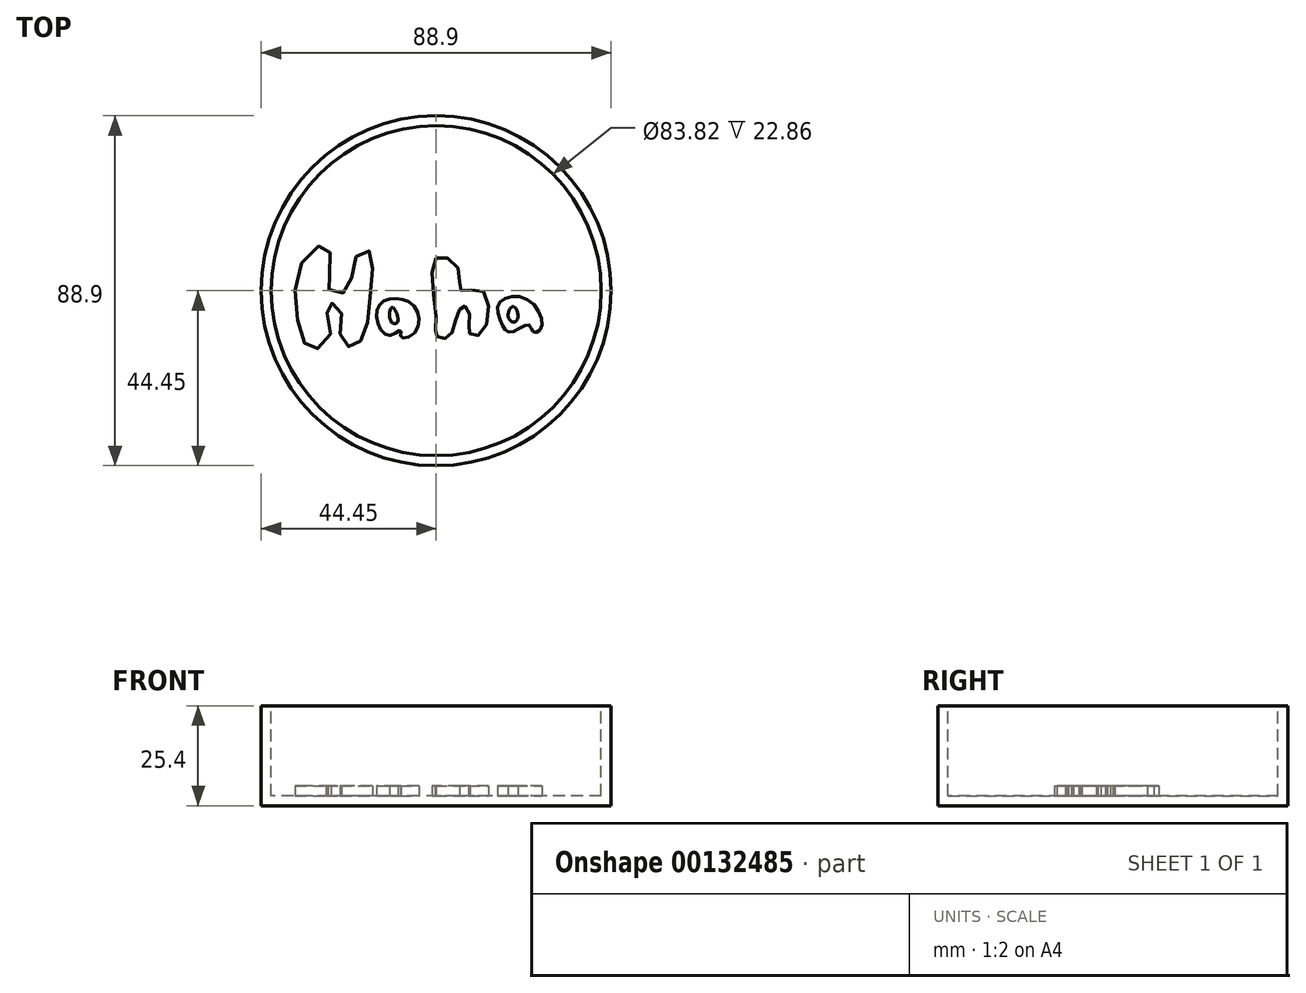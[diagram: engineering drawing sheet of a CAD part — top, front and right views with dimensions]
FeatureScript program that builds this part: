
annotation { "Feature Type Name" : "Feature", "Feature Type Description" : "" }
export const myFeature = defineFeature(function(context is Context, id is Id, definition is map)
    precondition{}
    {
        {
            var Q0;
            Q0=qCreatedBy(makeId("Top.planeOp"),FACE);
            var sketch = newSketch(context, id + "F0", { "sketchPlane" : qUnion([Q0])});
            skCircle(sketch, "E0", {"center": v(0, 0) * mm, "radius": 44.45 * mm});
            skSolve(sketch);
        }
        {
            var Q0;
            Q0=makeQuery(id+"F0.imprint","IMPRINT",FACE,{"disambiguationData":[TD([[makeQuery(id+"F0.imprint","IMPRINT",EDGE,{"derivedFrom":sQuery(id+"F0.wireOp",EDGE,"E0")}),1.0]])]});
            extrude(context, id + "F1", {"entities" : qUnion([Q0]), "oppositeDirection" : true, "depth" : 25.4 * mm});
        }
        {
            var Q0;
            Q0=makeQuery(id+"F1.opExtrude","CAP_FACE",FACE,{"disambiguationData":[OSD([sQuery(id+"F0.wireOp",EDGE,"E0")])],"isStart":true});
            shell(context, id + "F2", {"entities" : qUnion([Q0]), "thickness" : 2.54 * mm});
        }
        {
            var Q0;
            {var subQ0=sQuery(id+"F0.wireOp",EDGE,"E0");Q0=makeQuery(id+"F2.opShell","OFFSET_FACE",FACE,{"disambiguationData":[OSD([subQ0]),TDD([makeQuery(id+"F1.opExtrude","CAP_FACE",FACE,{"disambiguationData":[OSD([subQ0])],"isStart":false})])]});}
            var sketch = newSketch(context, id + "F3", { "sketchPlane" : qUnion([Q0])});
            skFitSpline(sketch, "E1", {"points": [v(-34.25, 7.07) * mm, v(-34.85, -9.1) * mm, v(-31.42, -14.95) * mm, v(-26.77, -10.5) * mm, v(-27.78, -3.64) * mm, v(-24.55, -4.04) * mm, v(-24.35, -11.11) * mm, v(-21.72, -14.35) * mm, v(-18.49, -11.52) * mm, v(-16.67, 0) * mm, v(-17.07, 10.1) * mm, v(-20.5, 8.28) * mm, v(-22.53, 0) * mm, v(-26.97, 0) * mm, v(-27.18, 3.23) * mm, v(-27.78, 11.31) * mm, v(-34.25, 7.07) * mm]});
            skFitSpline(sketch, "E2", {"points": [v(-10.2, -2.02) * mm, v(-14.45, -3.64) * mm, v(-14.65, -8.69) * mm, v(-11.62, -11.31) * mm, v(-9, -10.1) * mm, v(-9, -11.72) * mm, v(-5.35, -10.5) * mm, v(-5.35, -4.24) * mm, v(-10.2, -2.02) * mm]});
            skFitSpline(sketch, "E3", {"points": [v(-11.21, -4.24) * mm, v(-11.42, -7.88) * mm, v(-9.8, -7.88) * mm, v(-11.21, -4.24) * mm]});
            skFitSpline(sketch, "E4", {"points": [v(0, 8.28) * mm, v(0, -7.88) * mm, v(0, -11.52) * mm, v(2.93, -11.92) * mm, v(5.15, -6.87) * mm, v(6.97, -3.84) * mm, v(8.59, -6.67) * mm, v(8.38, -10.7) * mm, v(11.62, -10.7) * mm, v(11.82, 0) * mm, v(6.36, 0) * mm, v(5.56, 5.66) * mm, v(0, 8.28) * mm]});
            skFitSpline(sketch, "E5", {"points": [v(23.13, -2.22) * mm, v(16.06, -3.03) * mm, v(16.67, -8.49) * mm, v(18.9, -10.5) * mm, v(23.54, -8.69) * mm, v(24.75, -10.5) * mm, v(26.77, -9.3) * mm, v(23.13, -2.22) * mm]});
            skFitSpline(sketch, "E6", {"points": [v(19.7, -4.04) * mm, v(18.29, -5.86) * mm, v(19.3, -7.88) * mm, v(20.7, -7.07) * mm, v(19.7, -4.04) * mm]});
            skSolve(sketch);
        }
        {
            var Q0;
            Q0 = qSketchRegion(id + "F3", true);
            extrude(context, id + "F4", {"entities" : qUnion([Q0]), "operationType" : NewBodyOperationType.ADD, "depth" : 2.54 * mm});
        }
    });
